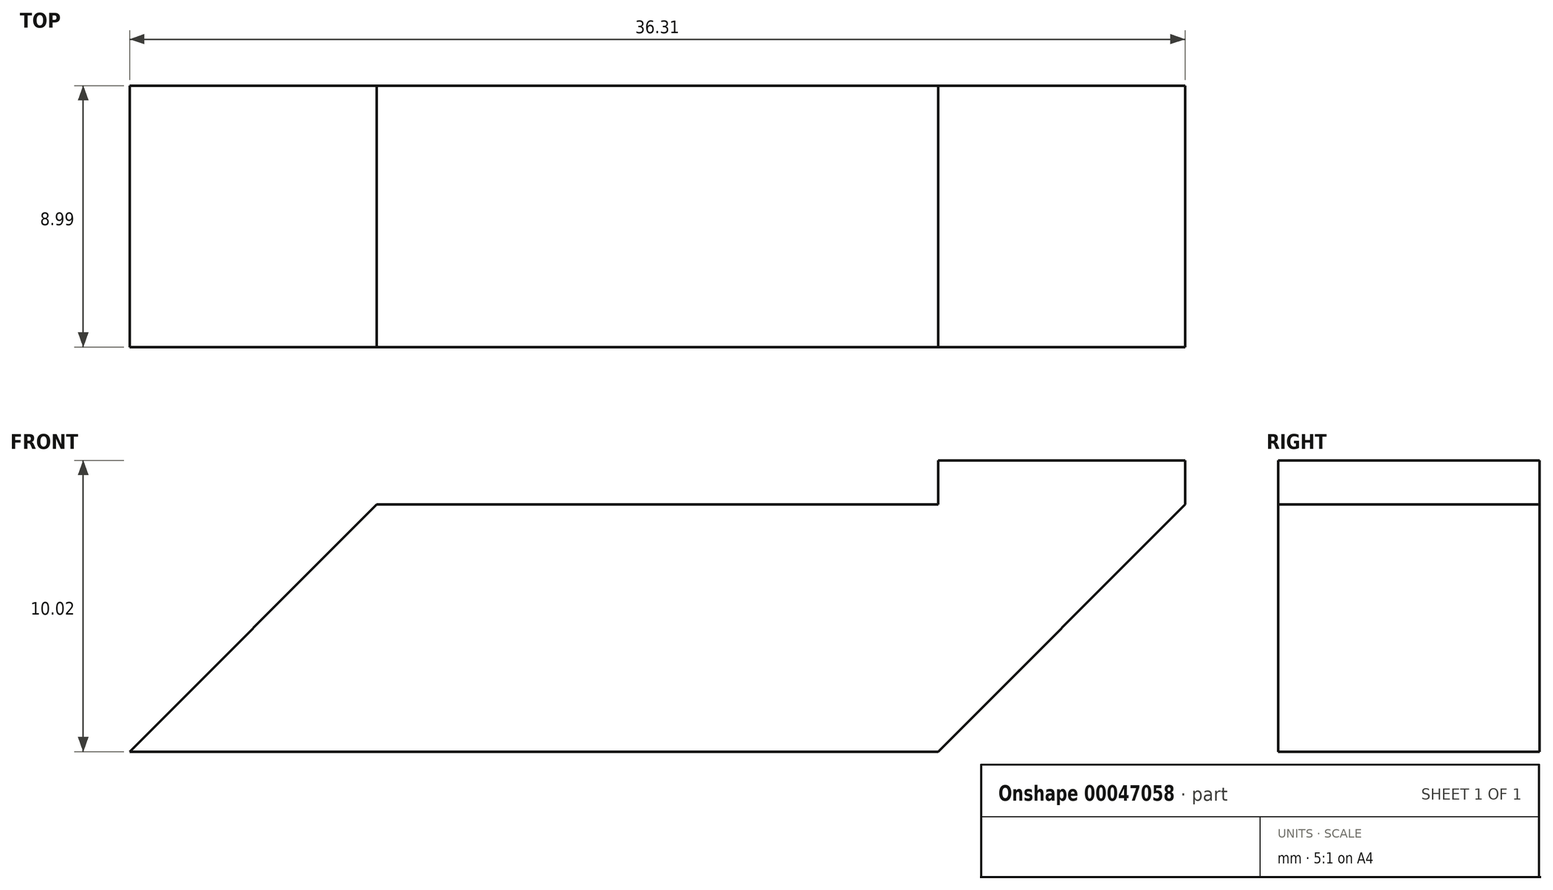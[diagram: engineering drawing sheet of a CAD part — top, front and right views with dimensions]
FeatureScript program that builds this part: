
annotation { "Feature Type Name" : "Feature", "Feature Type Description" : "" }
export const myFeature = defineFeature(function(context is Context, id is Id, definition is map)
    precondition{}
    {
        {
            var Q0;
            Q0=qCreatedBy(makeId("Front.planeOp"),FACE);
            var sketch = newSketch(context, id + "F0", { "sketchPlane" : qUnion([Q0])});
            skLineSegment(sketch, "E0", {"start": v(0, 0) * mm, "end": v(8.5, 8.5) * mm});
            skLineSegment(sketch, "E1", {"start": v(8.5, 8.5) * mm, "end": v(27.81, 8.5) * mm});
            skLineSegment(sketch, "E2", {"start": v(27.81, 8.5) * mm, "end": v(27.81, 10.02) * mm});
            skLineSegment(sketch, "E3", {"start": v(27.81, 10.02) * mm, "end": v(36.31, 10.02) * mm});
            skLineSegment(sketch, "E4", {"start": v(36.31, 10.02) * mm, "end": v(36.31, 8.5) * mm});
            skLineSegment(sketch, "E5", {"start": v(36.31, 8.5) * mm, "end": v(27.81, 0) * mm});
            skLineSegment(sketch, "E6", {"start": v(27.81, 0) * mm, "end": v(0, 0) * mm});
            skSolve(sketch);
        }
        {
            var Q0;
            Q0 = qSketchRegion(id + "F0", true);
            extrude(context, id + "F1", {"entities" : qUnion([Q0]), "depth" : 9 * mm});
        }
    });
